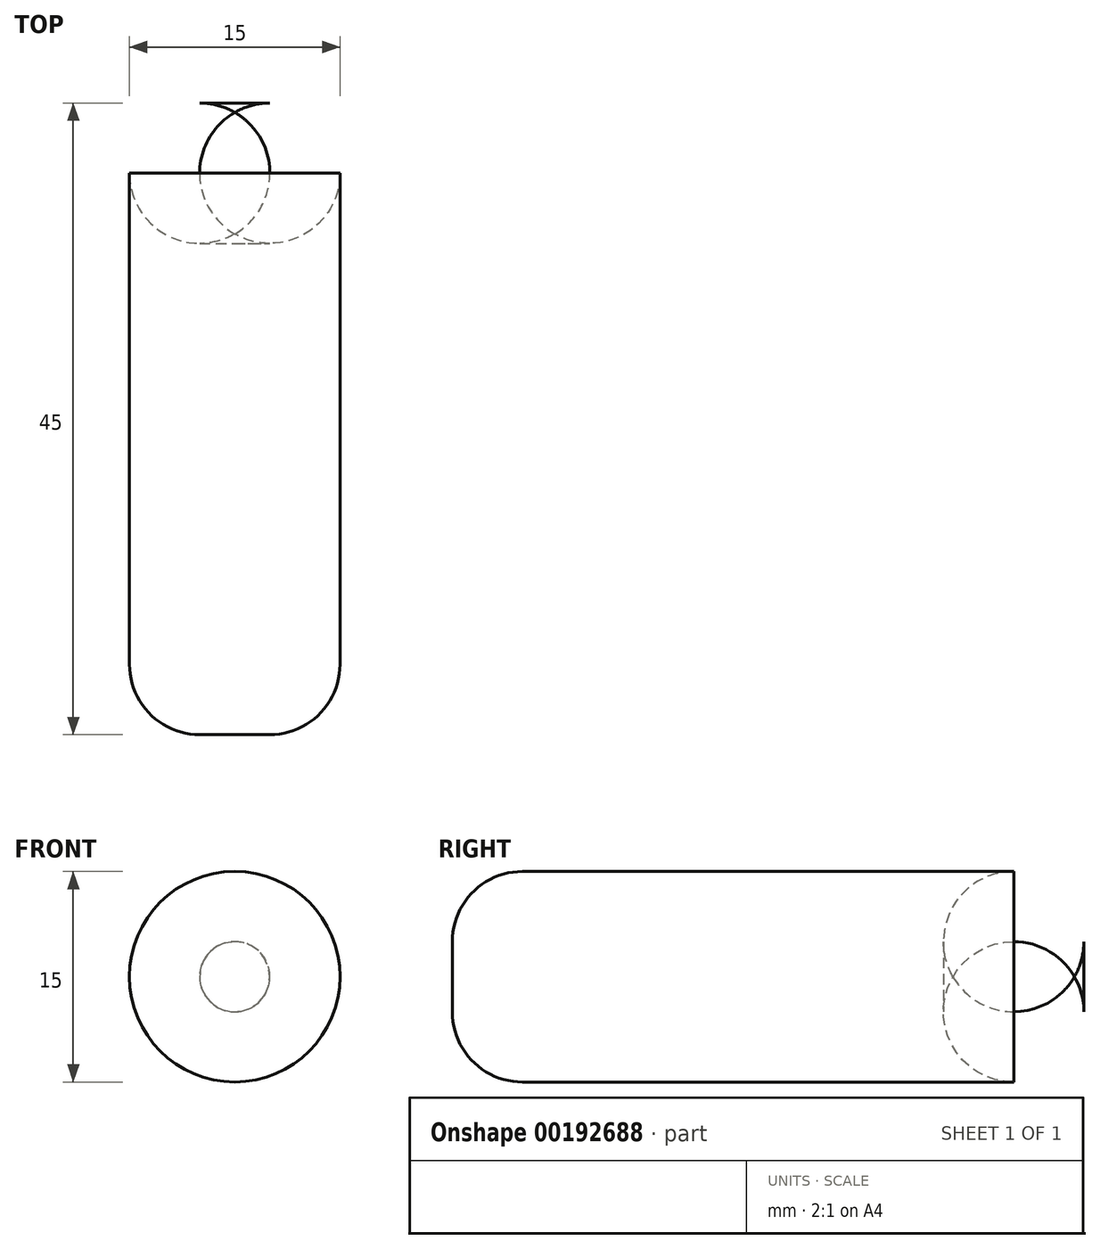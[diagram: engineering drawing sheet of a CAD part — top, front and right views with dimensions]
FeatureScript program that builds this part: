
annotation { "Feature Type Name" : "Feature", "Feature Type Description" : "" }
export const myFeature = defineFeature(function(context is Context, id is Id, definition is map)
    precondition{}
    {
        {
            var Q0;
            Q0=qCreatedBy(makeId("Front.planeOp"),FACE);
            var sketch = newSketch(context, id + "F0", { "sketchPlane" : qUnion([Q0])});
            skCircle(sketch, "E0", {"center": v(0, 0) * mm, "radius": 7.5 * mm});
            skSolve(sketch);
        }
        {
            var Q0;
            Q0=makeQuery(id+"F0.imprint","IMPRINT",FACE,{"disambiguationData":[TD([[makeQuery(id+"F0.imprint","IMPRINT",EDGE,{"derivedFrom":sQuery(id+"F0.wireOp",EDGE,"E0")}),1.0]])]});
            extrude(context, id + "F1", {"entities" : qUnion([Q0]), "endBound" : BoundingType.SYMMETRIC, "depth" : 45 * mm});
        }
        {
            var Q0;
            Q0=makeQuery(id+"F1.opExtrude","CAP_FACE",FACE,{"disambiguationData":[OSD([sQuery(id+"F0.wireOp",EDGE,"E0")])],"isStart":false});
            var Q1;
            Q1=makeQuery(id+"F1.opExtrude","CAP_EDGE",EDGE,{"disambiguationData":[OSD([sQuery(id+"F0.wireOp",EDGE,"E0")])],"isStart":true});
            fillet(context, id + "F2", {"entities" : qUnion([Q0, Q1]), "radius" : 5 * mm, "tangentPropagation" : true, "allowEdgeOverflow" : false});
        }
    });
